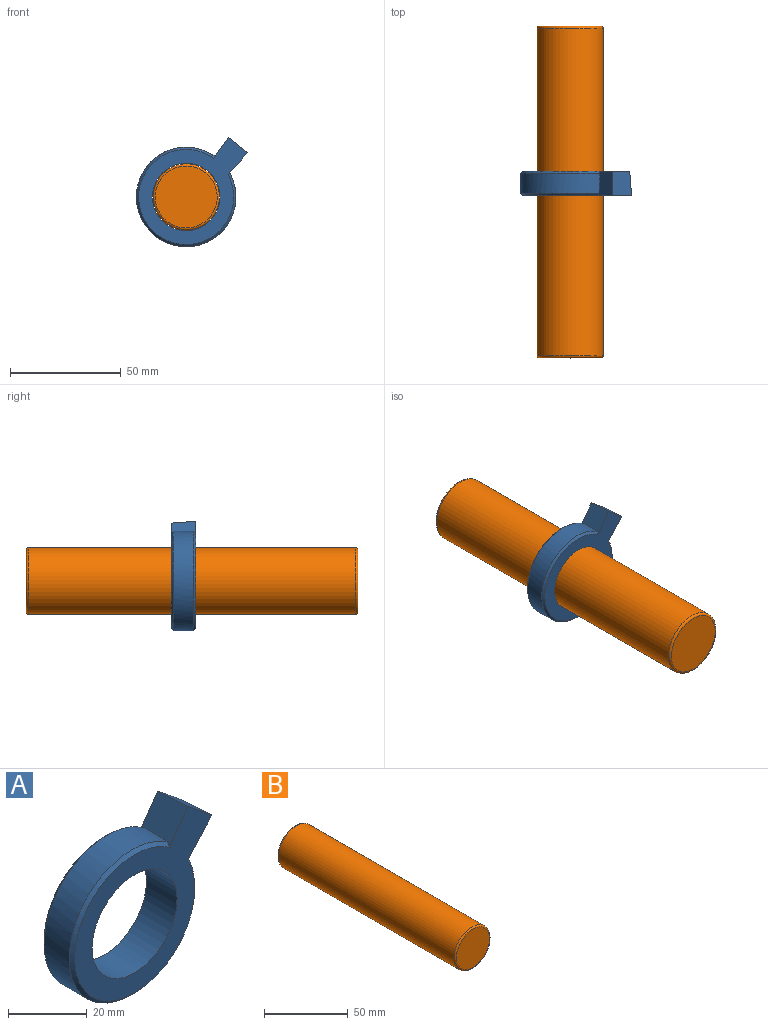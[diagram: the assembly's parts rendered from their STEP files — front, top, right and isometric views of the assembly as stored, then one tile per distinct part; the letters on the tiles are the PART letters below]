
ASSEMBLY  parts=2 mates=1
PART A: 9 faces, bbox 50.3x11x49.5 mm
  f0: cylinder r=22.5mm len=45mm, axis (0,1,0), area 1187.1mm2, adj f1,f2,f6,f8
  f1: cone r=21.5mm half-angle=45deg, axis (0,1,0), area 181.4mm2, adj f0,f4,f6,f8
  f2: cone r=22.5mm half-angle=45deg, axis (0,-1,0), area 182.9mm2, adj f0,f5,f6,f8
  f3: cylinder r=15.25mm len=30.5mm, axis (0,1,0), area 1054mm2, adj f4,f5
  f4: plane 49.26x48.5mm, normal (0,-1,0), area 846.9mm2, adj f1,f3,f6,f7,f8
  f5: plane 48.43x47.66mm, normal (0,1,0), area 826.9mm2, adj f2,f3,f6,f7,f8
  f6: plane 11.02x9.87mm, normal (0.74,0.05,-0.67), area 130.5mm2, adj f0,f1,f2,f4,f5,f7
  f7: plane 11x8.64mm, normal (0.63,0.05,0.78), area 115.8mm2, adj f4,f5,f6,f8
  f8: plane 11x9.8mm, normal (-0.82,0.05,0.58), area 114.2mm2, adj f0,f1,f2,f4,f5,f7
PART B: 5 faces, bbox 32.5x150x32.5 mm
  f0: cylinder r=15mm len=148mm, axis (0,1,0), area 13948.7mm2, adj f3,f4
  f1: plane 28x28mm, normal (0,-1,0), area 615.8mm2, adj f4
  f2: plane 28x28mm, normal (0,1,0), area 615.8mm2, adj f3
  f3: torus R=14mm, axis (0,-1,0), area 144.5mm2, adj f0,f2
  f4: torus R=14mm, axis (0,-1,0), area 144.5mm2, adj f0,f1
PLACE A t=(21.14,20.44,-12.95)mm
PLACE B t=(21.14,11.04,-12.95)mm fixed
MATE slider A.f0 <-> B.f0  axis (0,1,0) through (21.14,10.44,-12.95)mm
